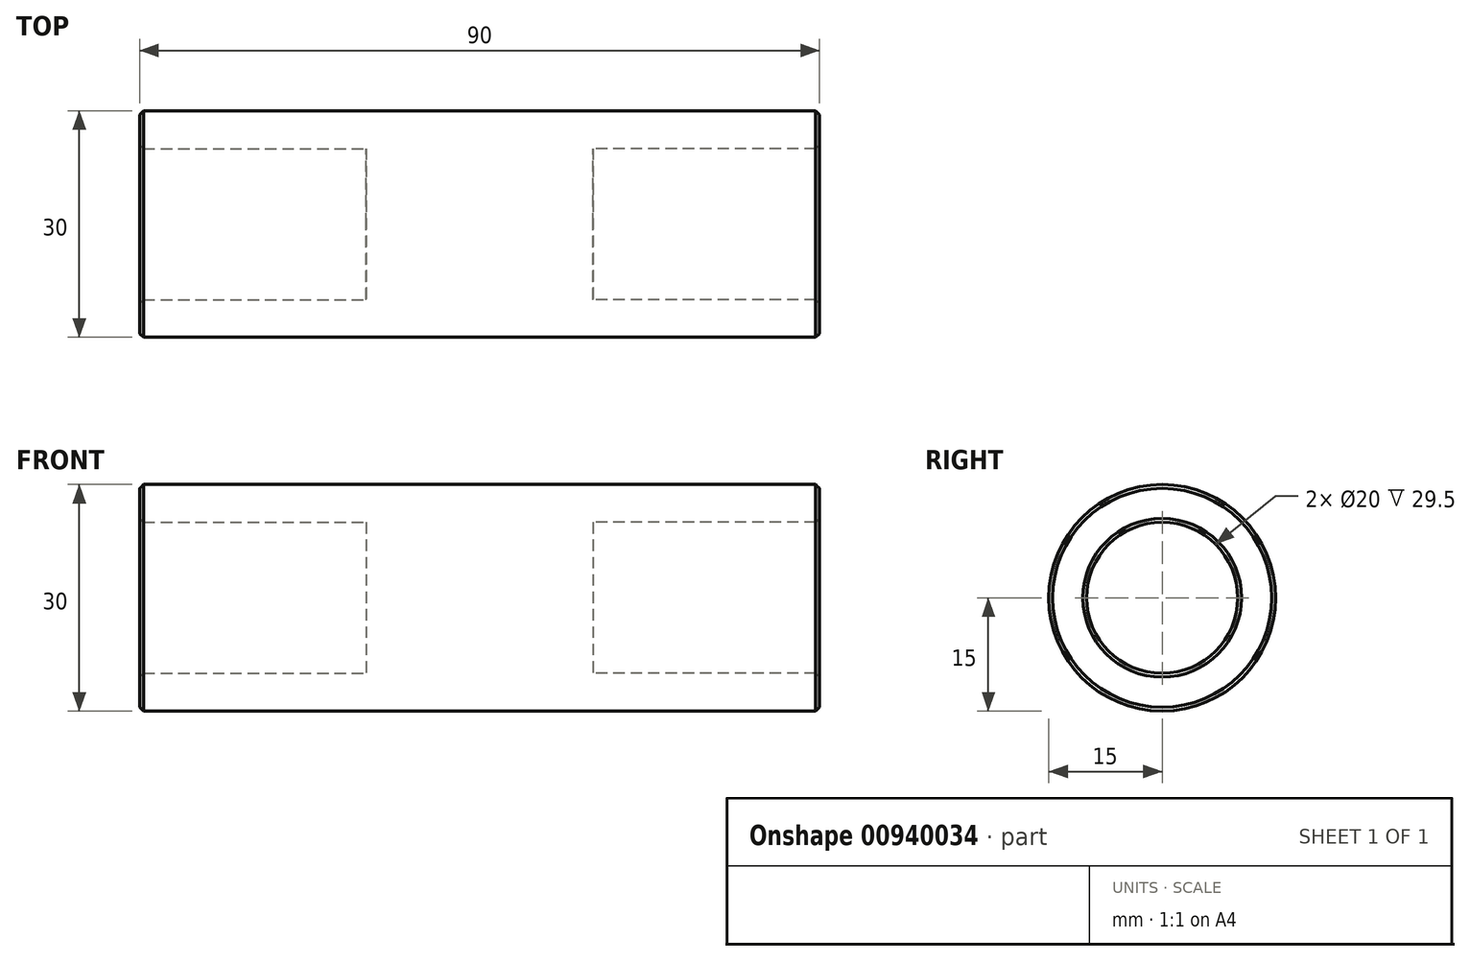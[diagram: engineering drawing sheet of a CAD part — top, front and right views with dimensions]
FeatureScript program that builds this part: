
annotation { "Feature Type Name" : "Feature", "Feature Type Description" : "" }
export const myFeature = defineFeature(function(context is Context, id is Id, definition is map)
    precondition{}
    {
        {
            var Q0;
            Q0=qCreatedBy(makeId("Top.planeOp"),FACE);
            var sketch = newSketch(context, id + "F0", { "sketchPlane" : qUnion([Q0])});
            skLineSegment(sketch, "E0", {"start": v(0, 0) * mm, "end": v(47.53, 0) * mm, "construction": true});
            skLineSegment(sketch, "E1", {"start": v(15, 0) * mm, "end": v(15, 10) * mm});
            skLineSegment(sketch, "E2", {"start": v(15, 10) * mm, "end": v(44.5, 10) * mm});
            skLineSegment(sketch, "E3", {"start": v(45, 10.5) * mm, "end": v(45, 14.5) * mm});
            skLineSegment(sketch, "E4", {"start": v(44.5, 15) * mm, "end": v(0, 15) * mm});
            skLineSegment(sketch, "E5", {"start": v(44.5, 10) * mm, "end": v(45, 10.5) * mm});
            skLineSegment(sketch, "E6", {"start": v(44.5, 15) * mm, "end": v(45, 14.5) * mm});
            skLineSegment(sketch, "E7", {"start": v(0, 0) * mm, "end": v(15, 0) * mm});
            skLineSegment(sketch, "E8", {"start": v(0, 15) * mm, "end": v(0, 0) * mm});
            skSolve(sketch);
        }
        {
            var Q0;
            Q0 = qSketchRegion(id + "F0", true);
            var Q1;
            Q1=sQuery(id+"F0.wireOp",EDGE,"E0");
            revolve(context, id + "F1", {"surfaceOperationType" : NewSurfaceOperationType.NEW, "entities" : qUnion([Q0]), "axis" : qUnion([Q1]), "revolveType" : RevolveType.FULL});
        }
        {
            var Q0;
            Q0=makeQuery(id+"F1.opRevolve","SWEPT_BODY",BODY,{"disambiguationData":[OSD([sQuery(id+"F0.wireOp",EDGE,"E1"),sQuery(id+"F0.wireOp",EDGE,"E2"),sQuery(id+"F0.wireOp",EDGE,"E3"),sQuery(id+"F0.wireOp",EDGE,"E4"),sQuery(id+"F0.wireOp",EDGE,"E5"),sQuery(id+"F0.wireOp",EDGE,"E6"),sQuery(id+"F0.wireOp",EDGE,"E7"),sQuery(id+"F0.wireOp",EDGE,"E8")])]});
            var Q1;
            Q1=qCreatedBy(makeId("Right.planeOp"),FACE);
            mirror(context, id + "F2", {"operationType" : NewBodyOperationType.ADD, "entities" : qUnion([Q0]), "mirrorPlane" : qUnion([Q1])});
        }
    });
